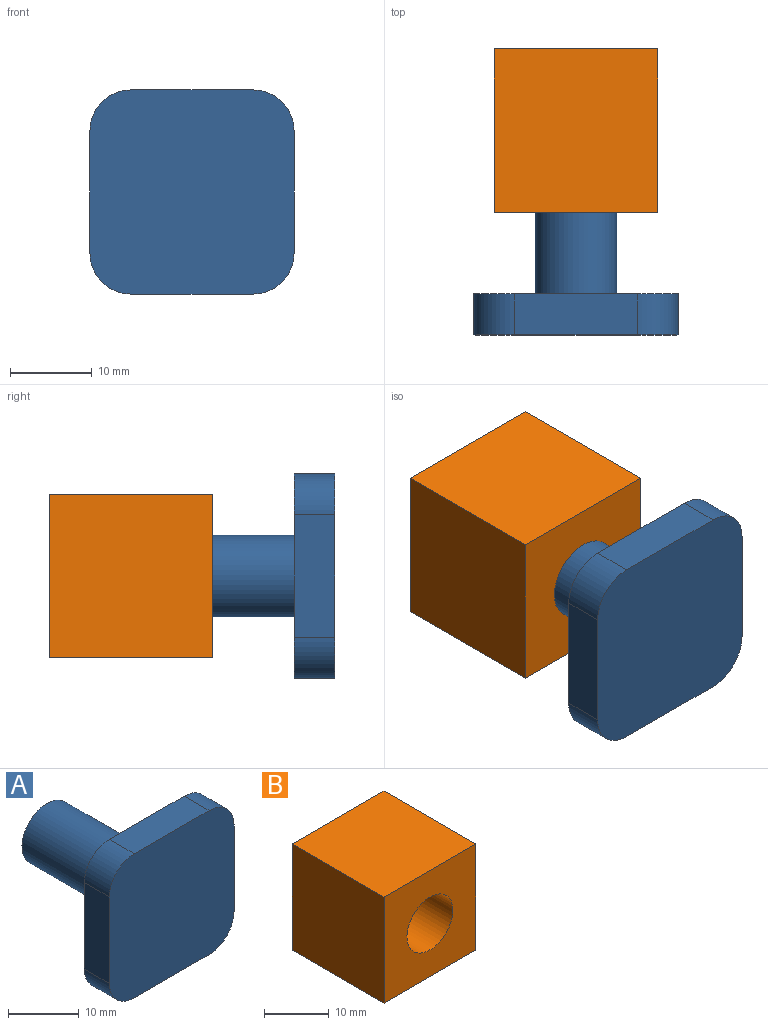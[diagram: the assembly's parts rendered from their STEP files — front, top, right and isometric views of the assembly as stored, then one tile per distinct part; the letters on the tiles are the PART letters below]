
ASSEMBLY  parts=2 mates=1
PART A: 12 faces, bbox 25x25x25 mm
  f0: cylinder r=5mm len=20mm, axis (0,1,0), area 628.3mm2, adj f1,f7
  f1: plane 10x10mm, normal (0,1,0), area 78.5mm2, adj f0
  f2: plane 15x5mm, normal (0,0,-1), area 75mm2, adj f6,f7,f8,f11
  f3: plane 15x5mm, normal (1,0,0), area 75mm2, adj f6,f7,f8,f9
  f4: plane 15x5mm, normal (0,0,1), area 75mm2, adj f6,f7,f9,f10
  f5: plane 15x5mm, normal (-1,0,0), area 75mm2, adj f6,f7,f10,f11
  f6: plane 25x25mm, normal (0,-1,0), area 603.5mm2, adj f2,f3,f4,f5,f8,f9,f10,f11
  f7: plane 25x25mm, normal (0,1,0), area 525mm2, adj f0,f2,f3,f4,f5,f8,f9,f10
  f8: cylinder r=5mm len=5mm, axis (0,-1,0), area 39.3mm2, adj f2,f3,f6,f7
  f9: cylinder r=5mm len=5mm, axis (0,1,0), area 39.3mm2, adj f3,f4,f6,f7
  f10: cylinder r=5mm len=5mm, axis (0,-1,0), area 39.3mm2, adj f4,f5,f6,f7
  f11: cylinder r=5mm len=5mm, axis (0,1,0), area 39.3mm2, adj f2,f5,f6,f7
PART B: 8 faces, bbox 20x20x20 mm
  f0: plane 20x20mm, normal (-1,0,0), area 400mm2, adj f1,f3,f4,f5
  f1: plane 20x20mm, normal (0,-1,0), area 321.5mm2, adj f0,f2,f4,f5,f7
  f2: plane 20x20mm, normal (1,0,0), area 400mm2, adj f1,f3,f4,f5
  f3: plane 20x20mm, normal (0,1,0), area 400mm2, adj f0,f2,f4,f5
  f4: plane 20x20mm, normal (0,0,1), area 400mm2, adj f0,f1,f2,f3
  f5: plane 20x20mm, normal (0,0,-1), area 400mm2, adj f0,f1,f2,f3
  f6: cone r=0mm half-angle=59deg, axis (0,-1,0), area 91.6mm2, adj f7
  f7: cylinder r=5mm len=10mm, axis (0,-1,0), area 314.2mm2, adj f1,f6
PLACE A t=(-43.75,-23.3,18.6)mm
PLACE B t=(-53.75,-33.3,8.6)mm
MATE fastened B.f6 <-> A.f0  axis (0,-1,0) through (-43.75,-23.3,18.6)mm
